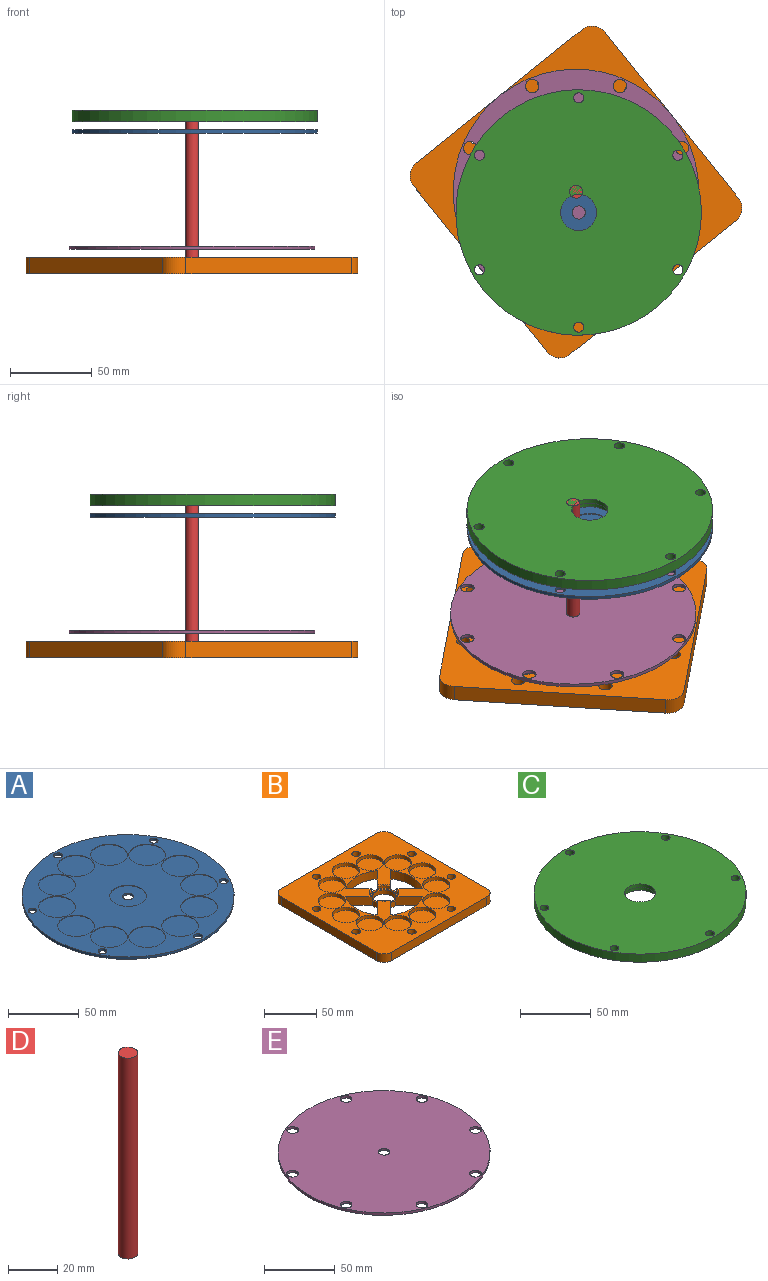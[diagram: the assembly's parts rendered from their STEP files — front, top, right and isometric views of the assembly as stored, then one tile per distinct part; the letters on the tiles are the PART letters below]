
ASSEMBLY  parts=5 mates=7
PART A: 36 faces, bbox 150x150x2 mm
  f0: cylinder r=4mm len=8mm, axis (0,0,-1), area 37.7mm2, adj f9,f19
  f1: cylinder r=3.1mm len=6.2mm, axis (0,0,-1), area 39mm2, adj f8,f9
  f2: cylinder r=3.1mm len=6.2mm, axis (0,0,-1), area 39mm2, adj f8,f9
  f3: cylinder r=3.1mm len=6.2mm, axis (0,0,-1), area 39mm2, adj f8,f9
  f4: cylinder r=3.1mm len=6.2mm, axis (0,0,-1), area 39mm2, adj f8,f9
  f5: cylinder r=3.1mm len=6.2mm, axis (0,0,-1), area 39mm2, adj f8,f9
  f6: cylinder r=3.1mm len=6.2mm, axis (0,0,-1), area 39mm2, adj f8,f9
  f7: cylinder r=75mm len=150mm, axis (0,0,-1), area 942.5mm2, adj f8,f9
  f8: plane 150x150mm, normal (0,0,1), area 10588.2mm2, adj f1,f2,f3,f4,f5,f6,f7,f10
  f9: plane 150x150mm, normal (0,0,-1), area 17440mm2, adj f0,f1,f2,f3,f4,f5,f6,f7
  f10: cylinder r=13mm len=26mm, axis (0,0,1), area 40.8mm2, adj f8,f11
  f11: plane 26x26mm, normal (0,0,1), area 530.9mm2, adj f10
  f12: cylinder r=13mm len=26mm, axis (0,0,1), area 40.8mm2, adj f8,f13
  f13: plane 26x26mm, normal (0,0,1), area 530.9mm2, adj f12
  f14: cylinder r=13mm len=26mm, axis (0,0,1), area 40.8mm2, adj f8,f15
  f15: plane 26x26mm, normal (0,0,1), area 530.9mm2, adj f14
  f16: cylinder r=13mm len=26mm, axis (0,0,1), area 40.8mm2, adj f8,f17
  f17: plane 26x26mm, normal (0,0,1), area 530.9mm2, adj f16
  f18: cylinder r=13mm len=26mm, axis (0,0,1), area 40.8mm2, adj f8,f19
  f19: plane 26x26mm, normal (0,0,1), area 480.7mm2, adj f0,f18
  f20: cylinder r=13mm len=26mm, axis (0,0,1), area 40.8mm2, adj f8,f21
  f21: plane 26x26mm, normal (0,0,1), area 530.9mm2, adj f20
  f22: cylinder r=13mm len=26mm, axis (0,0,1), area 40.8mm2, adj f8,f23
  f23: plane 26x26mm, normal (0,0,1), area 530.9mm2, adj f22
  f24: cylinder r=13mm len=26mm, axis (0,0,1), area 40.8mm2, adj f8,f25
  f25: plane 26x26mm, normal (0,0,1), area 530.9mm2, adj f24
  f26: cylinder r=13mm len=26mm, axis (0,0,1), area 40.8mm2, adj f8,f27
  f27: plane 26x26mm, normal (0,0,1), area 530.9mm2, adj f26
  f28: cylinder r=13mm len=26mm, axis (0,0,1), area 40.8mm2, adj f8,f29
  f29: plane 26x26mm, normal (0,0,1), area 530.9mm2, adj f28
  f30: cylinder r=13mm len=26mm, axis (0,0,1), area 40.8mm2, adj f8,f31
  f31: plane 26x26mm, normal (0,0,1), area 530.9mm2, adj f30
  f32: cylinder r=13mm len=26mm, axis (0,0,1), area 40.8mm2, adj f8,f33
  f33: plane 26x26mm, normal (0,0,1), area 530.9mm2, adj f32
  f34: cylinder r=13mm len=26mm, axis (0,0,1), area 40.8mm2, adj f8,f35
  f35: plane 26x26mm, normal (0,0,1), area 530.9mm2, adj f34
PART B: 70 faces, bbox 150x150x10 mm
  f0: cylinder r=13mm len=7.05mm, axis (0,0,-1), area 42.9mm2, adj f15,f16,f34,f63
  f1: cylinder r=13mm len=7.05mm, axis (0,0,-1), area 42.9mm2, adj f17,f18,f34,f63
  f2: cylinder r=13mm len=7.05mm, axis (0,0,-1), area 42.9mm2, adj f19,f20,f34,f63
  f3: cylinder r=13mm len=7.05mm, axis (0,0,-1), area 42.9mm2, adj f12,f14,f34,f63
  f4: cylinder r=11.1mm len=22.2mm, axis (0,0,-1), area 348.7mm2, adj f68,f69
  f5: plane 130x10mm, normal (1,0,0), area 1300mm2, adj f6,f32,f33,f34
  f6: cylinder r=10mm len=10mm, axis (0,0,-1), area 157.1mm2, adj f5,f7,f33,f34
  f7: plane 130x10mm, normal (0,1,0), area 1300mm2, adj f6,f8,f33,f34
  f8: cylinder r=10mm len=10mm, axis (0,0,-1), area 157.1mm2, adj f7,f9,f33,f34
  f9: plane 130x10mm, normal (-1,0,0), area 1300mm2, adj f8,f10,f33,f34
  f10: cylinder r=10mm len=10mm, axis (0,0,-1), area 157.1mm2, adj f9,f11,f33,f34
  f11: plane 130x10mm, normal (0,-1,0), area 1300mm2, adj f10,f32,f33,f34
  f12: plane 18.11x18.11mm, normal (-0.71,-0.71,0), area 255.9mm2, adj f3,f13,f33,f34,f62,f66
  f13: cylinder r=37.5mm len=43.28mm, axis (0,0,-1), area 461.4mm2, adj f12,f14,f33,f34
  f14: plane 18.11x18.11mm, normal (0.71,-0.71,0), area 255.9mm2, adj f3,f13,f33,f34,f59,f65
  f15: plane 18.11x18.11mm, normal (-0.71,-0.71,0), area 255.9mm2, adj f0,f29,f33,f34,f60,f64
  f16: plane 18.11x18.11mm, normal (-0.71,0.71,0), area 255.9mm2, adj f0,f29,f33,f34,f59,f65
  f17: plane 18.11x18.11mm, normal (-0.71,0.71,0), area 255.9mm2, adj f1,f30,f33,f34,f61,f67
  f18: plane 18.11x18.11mm, normal (0.71,0.71,0), area 255.9mm2, adj f1,f30,f33,f34,f60,f64
  f19: plane 18.11x18.11mm, normal (0.71,0.71,0), area 255.9mm2, adj f2,f31,f33,f34,f62,f66
  f20: plane 18.11x18.11mm, normal (0.71,-0.71,0), area 255.9mm2, adj f2,f31,f33,f34,f61,f67
  f21: cylinder r=4.1mm len=10mm, axis (0,0,-1), area 257.6mm2, adj f33,f34
  f22: cylinder r=4.1mm len=10mm, axis (0,0,-1), area 257.6mm2, adj f33,f34
  f23: cylinder r=4.1mm len=10mm, axis (0,0,-1), area 257.6mm2, adj f33,f34
  f24: cylinder r=4.1mm len=10mm, axis (0,0,-1), area 257.6mm2, adj f33,f34
  f25: cylinder r=4.1mm len=10mm, axis (0,0,-1), area 257.6mm2, adj f33,f34
  f26: cylinder r=4.1mm len=10mm, axis (0,0,-1), area 257.6mm2, adj f33,f34
  f27: cylinder r=4.1mm len=10mm, axis (0,0,-1), area 257.6mm2, adj f33,f34
  f28: cylinder r=4.1mm len=10mm, axis (0,0,-1), area 257.6mm2, adj f33,f34
  f29: cylinder r=37.5mm len=43.28mm, axis (0,0,-1), area 461.4mm2, adj f15,f16,f33,f34
  f30: cylinder r=37.5mm len=43.28mm, axis (0,0,-1), area 461.4mm2, adj f17,f18,f33,f34
  f31: cylinder r=37.5mm len=43.28mm, axis (0,0,-1), area 461.4mm2, adj f19,f20,f33,f34
  f32: cylinder r=10mm len=10mm, axis (0,0,-1), area 157.1mm2, adj f5,f11,f33,f34
  f33: plane 150x150mm, normal (0,0,1), area 12413.2mm2, adj f5,f6,f7,f8,f9,f10,f11,f12
  f34: plane 150x150mm, normal (0,0,-1), area 18945.5mm2, adj f0,f1,f2,f3,f5,f6,f7,f8
  f35: cylinder r=13mm len=26mm, axis (0,0,1), area 326.7mm2, adj f33,f36
  f36: plane 26x26mm, normal (0,0,1), area 530.9mm2, adj f35
  f37: cylinder r=13mm len=26mm, axis (0,0,1), area 326.7mm2, adj f33,f38
  f38: plane 26x26mm, normal (0,0,1), area 530.9mm2, adj f37
  f39: cylinder r=13mm len=26mm, axis (0,0,1), area 326.7mm2, adj f33,f40
  f40: plane 26x26mm, normal (0,0,1), area 530.9mm2, adj f39
  f41: cylinder r=13mm len=26mm, axis (0,0,1), area 326.7mm2, adj f33,f42
  f42: plane 26x26mm, normal (0,0,1), area 530.9mm2, adj f41
  f43: cylinder r=13mm len=26mm, axis (0,0,1), area 326.7mm2, adj f33,f44
  f44: plane 26x26mm, normal (0,0,1), area 530.9mm2, adj f43
  f45: cylinder r=13mm len=26mm, axis (0,0,1), area 326.7mm2, adj f33,f46
  f46: plane 26x26mm, normal (0,0,1), area 530.9mm2, adj f45
  f47: cylinder r=13mm len=26mm, axis (0,0,1), area 326.7mm2, adj f33,f48
  f48: plane 26x26mm, normal (0,0,1), area 530.9mm2, adj f47
  f49: cylinder r=13mm len=26mm, axis (0,0,1), area 326.7mm2, adj f33,f50
  f50: plane 26x26mm, normal (0,0,1), area 530.9mm2, adj f49
  f51: cylinder r=13mm len=26mm, axis (0,0,1), area 326.7mm2, adj f33,f52
  f52: plane 26x26mm, normal (0,0,1), area 530.9mm2, adj f51
  f53: cylinder r=13mm len=26mm, axis (0,0,1), area 326.7mm2, adj f33,f54
  f54: plane 26x26mm, normal (0,0,1), area 530.9mm2, adj f53
  f55: cylinder r=13mm len=26mm, axis (0,0,1), area 326.7mm2, adj f33,f56
  f56: plane 26x26mm, normal (0,0,1), area 530.9mm2, adj f55
  f57: cylinder r=13mm len=26mm, axis (0,0,1), area 326.7mm2, adj f33,f58
  f58: plane 26x26mm, normal (0,0,1), area 530.9mm2, adj f57
  f59: cylinder r=13mm len=8.99mm, axis (0,0,1), area 39.8mm2, adj f14,f16,f63,f65
  f60: cylinder r=13mm len=8.99mm, axis (0,0,1), area 39.8mm2, adj f15,f18,f63,f64
  f61: cylinder r=13mm len=8.99mm, axis (0,0,1), area 39.8mm2, adj f17,f20,f63,f67
  f62: cylinder r=13mm len=8.99mm, axis (0,0,1), area 39.8mm2, adj f12,f19,f63,f66
  f63: plane 26x26mm, normal (0,0,1), area 108.2mm2, adj f0,f1,f2,f3,f59,f60,f61,f62
  f64: torus R=14mm, axis (0,0,1), area 20.8mm2, adj f15,f18,f33,f60
  f65: torus R=14mm, axis (0,0,1), area 20.8mm2, adj f14,f16,f33,f59
  f66: torus R=14mm, axis (0,0,1), area 20.8mm2, adj f12,f19,f33,f62
  f67: torus R=14mm, axis (0,0,1), area 20.8mm2, adj f17,f20,f33,f61
  f68: cone r=11.1mm half-angle=45deg, axis (0,0,1), area 50.4mm2, adj f4,f63
  f69: cone r=11.6mm half-angle=45deg, axis (0,0,-1), area 50.4mm2, adj f4,f34
PART C: 36 faces, bbox 150x150x7 mm
  f0: cylinder r=11.05mm len=22.1mm, axis (0,0,-1), area 208.3mm2, adj f8,f19
  f1: cylinder r=3.1mm len=7mm, axis (0,0,-1), area 136.3mm2, adj f8,f9
  f2: cylinder r=3.1mm len=7mm, axis (0,0,-1), area 136.3mm2, adj f8,f9
  f3: cylinder r=3.1mm len=7mm, axis (0,0,-1), area 136.3mm2, adj f8,f9
  f4: cylinder r=3.1mm len=7mm, axis (0,0,-1), area 136.3mm2, adj f8,f9
  f5: cylinder r=3.1mm len=7mm, axis (0,0,-1), area 136.3mm2, adj f8,f9
  f6: cylinder r=3.1mm len=7mm, axis (0,0,-1), area 136.3mm2, adj f8,f9
  f7: cylinder r=75mm len=150mm, axis (0,0,-1), area 3298.7mm2, adj f8,f9
  f8: plane 150x150mm, normal (0,0,1), area 17106.7mm2, adj f0,f1,f2,f3,f4,f5,f6,f7
  f9: plane 150x150mm, normal (0,0,-1), area 10588.2mm2, adj f1,f2,f3,f4,f5,f6,f7,f10
  f10: cylinder r=13mm len=26mm, axis (0,0,-1), area 326.7mm2, adj f9,f11
  f11: plane 26x26mm, normal (0,0,-1), area 530.9mm2, adj f10
  f12: cylinder r=13mm len=26mm, axis (0,0,-1), area 326.7mm2, adj f9,f13
  f13: plane 26x26mm, normal (0,0,-1), area 530.9mm2, adj f12
  f14: cylinder r=13mm len=26mm, axis (0,0,-1), area 326.7mm2, adj f9,f15
  f15: plane 26x26mm, normal (0,0,-1), area 530.9mm2, adj f14
  f16: cylinder r=13mm len=26mm, axis (0,0,-1), area 326.7mm2, adj f9,f17
  f17: plane 26x26mm, normal (0,0,-1), area 530.9mm2, adj f16
  f18: cylinder r=13mm len=26mm, axis (0,0,-1), area 326.7mm2, adj f9,f19
  f19: plane 26x26mm, normal (0,0,-1), area 147.3mm2, adj f0,f18
  f20: cylinder r=13mm len=26mm, axis (0,0,-1), area 326.7mm2, adj f9,f21
  f21: plane 26x26mm, normal (0,0,-1), area 530.9mm2, adj f20
  f22: cylinder r=13mm len=26mm, axis (0,0,-1), area 326.7mm2, adj f9,f23
  f23: plane 26x26mm, normal (0,0,-1), area 530.9mm2, adj f22
  f24: cylinder r=13mm len=26mm, axis (0,0,-1), area 326.7mm2, adj f9,f25
  f25: plane 26x26mm, normal (0,0,-1), area 530.9mm2, adj f24
  f26: cylinder r=13mm len=26mm, axis (0,0,-1), area 326.7mm2, adj f9,f27
  f27: plane 26x26mm, normal (0,0,-1), area 530.9mm2, adj f26
  f28: cylinder r=13mm len=26mm, axis (0,0,-1), area 326.7mm2, adj f9,f29
  f29: plane 26x26mm, normal (0,0,-1), area 530.9mm2, adj f28
  f30: cylinder r=13mm len=26mm, axis (0,0,-1), area 326.7mm2, adj f9,f31
  f31: plane 26x26mm, normal (0,0,-1), area 530.9mm2, adj f30
  f32: cylinder r=13mm len=26mm, axis (0,0,-1), area 326.7mm2, adj f9,f33
  f33: plane 26x26mm, normal (0,0,-1), area 530.9mm2, adj f32
  f34: cylinder r=13mm len=26mm, axis (0,0,-1), area 326.7mm2, adj f9,f35
  f35: plane 26x26mm, normal (0,0,-1), area 530.9mm2, adj f34
PART D: 3 faces, bbox 7.9x7.9x100 mm
  f0: cylinder r=3.95mm len=100mm, axis (0,0,-1), area 2481.9mm2, adj f1,f2
  f1: plane 7.9x7.9mm, normal (0,0,1), area 49mm2, adj f0
  f2: plane 7.9x7.9mm, normal (0,0,-1), area 49mm2, adj f0
PART E: 38 faces, bbox 150x150x2 mm
  f0: cylinder r=4mm len=8mm, axis (0,0,-1), area 37.7mm2, adj f10,f21
  f1: cylinder r=4.1mm len=8.2mm, axis (0,0,-1), area 51.5mm2, adj f10,f11
  f2: cylinder r=4.1mm len=8.2mm, axis (0,0,-1), area 51.5mm2, adj f10,f11
  f3: cylinder r=4.1mm len=8.2mm, axis (0,0,-1), area 51.5mm2, adj f10,f11
  f4: cylinder r=4.1mm len=8.2mm, axis (0,0,-1), area 51.5mm2, adj f10,f11
  f5: cylinder r=4.1mm len=8.2mm, axis (0,0,-1), area 51.5mm2, adj f10,f11
  f6: cylinder r=4.1mm len=8.2mm, axis (0,0,-1), area 51.5mm2, adj f10,f11
  f7: cylinder r=4.1mm len=8.2mm, axis (0,0,-1), area 51.5mm2, adj f10,f11
  f8: cylinder r=4.1mm len=8.2mm, axis (0,0,-1), area 51.5mm2, adj f10,f11
  f9: cylinder r=75mm len=150mm, axis (0,0,-1), area 942.5mm2, adj f10,f11
  f10: plane 150x150mm, normal (0,0,1), area 17198.7mm2, adj f0,f1,f2,f3,f4,f5,f6,f7
  f11: plane 150x150mm, normal (0,0,-1), area 10346.9mm2, adj f1,f2,f3,f4,f5,f6,f7,f8
  f12: cylinder r=13mm len=26mm, axis (0,0,-1), area 40.8mm2, adj f11,f13
  f13: plane 26x26mm, normal (0,0,-1), area 530.9mm2, adj f12
  f14: cylinder r=13mm len=26mm, axis (0,0,-1), area 40.8mm2, adj f11,f15
  f15: plane 26x26mm, normal (0,0,-1), area 530.9mm2, adj f14
  f16: cylinder r=13mm len=26mm, axis (0,0,-1), area 40.8mm2, adj f11,f17
  f17: plane 26x26mm, normal (0,0,-1), area 530.9mm2, adj f16
  f18: cylinder r=13mm len=26mm, axis (0,0,-1), area 40.8mm2, adj f11,f19
  f19: plane 26x26mm, normal (0,0,-1), area 530.9mm2, adj f18
  f20: cylinder r=13mm len=26mm, axis (0,0,-1), area 40.8mm2, adj f11,f21
  f21: plane 26x26mm, normal (0,0,-1), area 480.7mm2, adj f0,f20
  f22: cylinder r=13mm len=26mm, axis (0,0,-1), area 40.8mm2, adj f11,f23
  f23: plane 26x26mm, normal (0,0,-1), area 530.9mm2, adj f22
  f24: cylinder r=13mm len=26mm, axis (0,0,-1), area 40.8mm2, adj f11,f25
  f25: plane 26x26mm, normal (0,0,-1), area 530.9mm2, adj f24
  f26: cylinder r=13mm len=26mm, axis (0,0,-1), area 40.8mm2, adj f11,f27
  f27: plane 26x26mm, normal (0,0,-1), area 530.9mm2, adj f26
  f28: cylinder r=13mm len=26mm, axis (0,0,-1), area 40.8mm2, adj f11,f29
  f29: plane 26x26mm, normal (0,0,-1), area 530.9mm2, adj f28
  f30: cylinder r=13mm len=26mm, axis (0,0,-1), area 40.8mm2, adj f11,f31
  f31: plane 26x26mm, normal (0,0,-1), area 530.9mm2, adj f30
  f32: cylinder r=13mm len=26mm, axis (0,0,-1), area 40.8mm2, adj f11,f33
  f33: plane 26x26mm, normal (0,0,-1), area 530.9mm2, adj f32
  f34: cylinder r=13mm len=26mm, axis (0,0,-1), area 40.8mm2, adj f11,f35
  f35: plane 26x26mm, normal (0,0,-1), area 530.9mm2, adj f34
  f36: cylinder r=13mm len=26mm, axis (0,0,-1), area 40.8mm2, adj f11,f37
  f37: plane 26x26mm, normal (0,0,-1), area 530.9mm2, adj f36
PLACE A t=(0.14,0.1,132.43)mm
PLACE B rot(axis=(0,0,-1),51.2deg) t=(-1.48,12.77,46.43)mm
PLACE C rot(axis=(0,0,1),0deg) t=(0.14,0.1,139.43)mm
PLACE D rot(axis=(0,0,1),0deg) t=(-1.48,12.77,46.43)mm
PLACE E rot(axis=(0,0,1),0deg) t=(-1.48,12.77,61.43)mm
MATE planar C.f7 <-> A.f7  axis (0,0,-1) through (0.14,0.1,139.43)mm
MATE planar D.f0 <-> C.f7  axis (0,0,1) through (-1.48,12.77,146.43)mm
MATE planar B.f1 <-> E.f0  axis (0,0,1) through (-1.48,12.77,56.43)mm
MATE cylindrical D.f0 <-> B.f4  axis (0,0,-1) through (-1.48,12.77,96.43)mm
MATE cylindrical E.f0 <-> D.f0  axis (0,0,-1) through (-1.48,12.77,63.43)mm
MATE slider C.f0 <-> A.f0  axis (0,0,-1) through (0.14,0.1,146.43)mm
MATE planar D.f0 <-> B.f1  axis (0,0,-1) through (-1.48,12.77,46.43)mm
